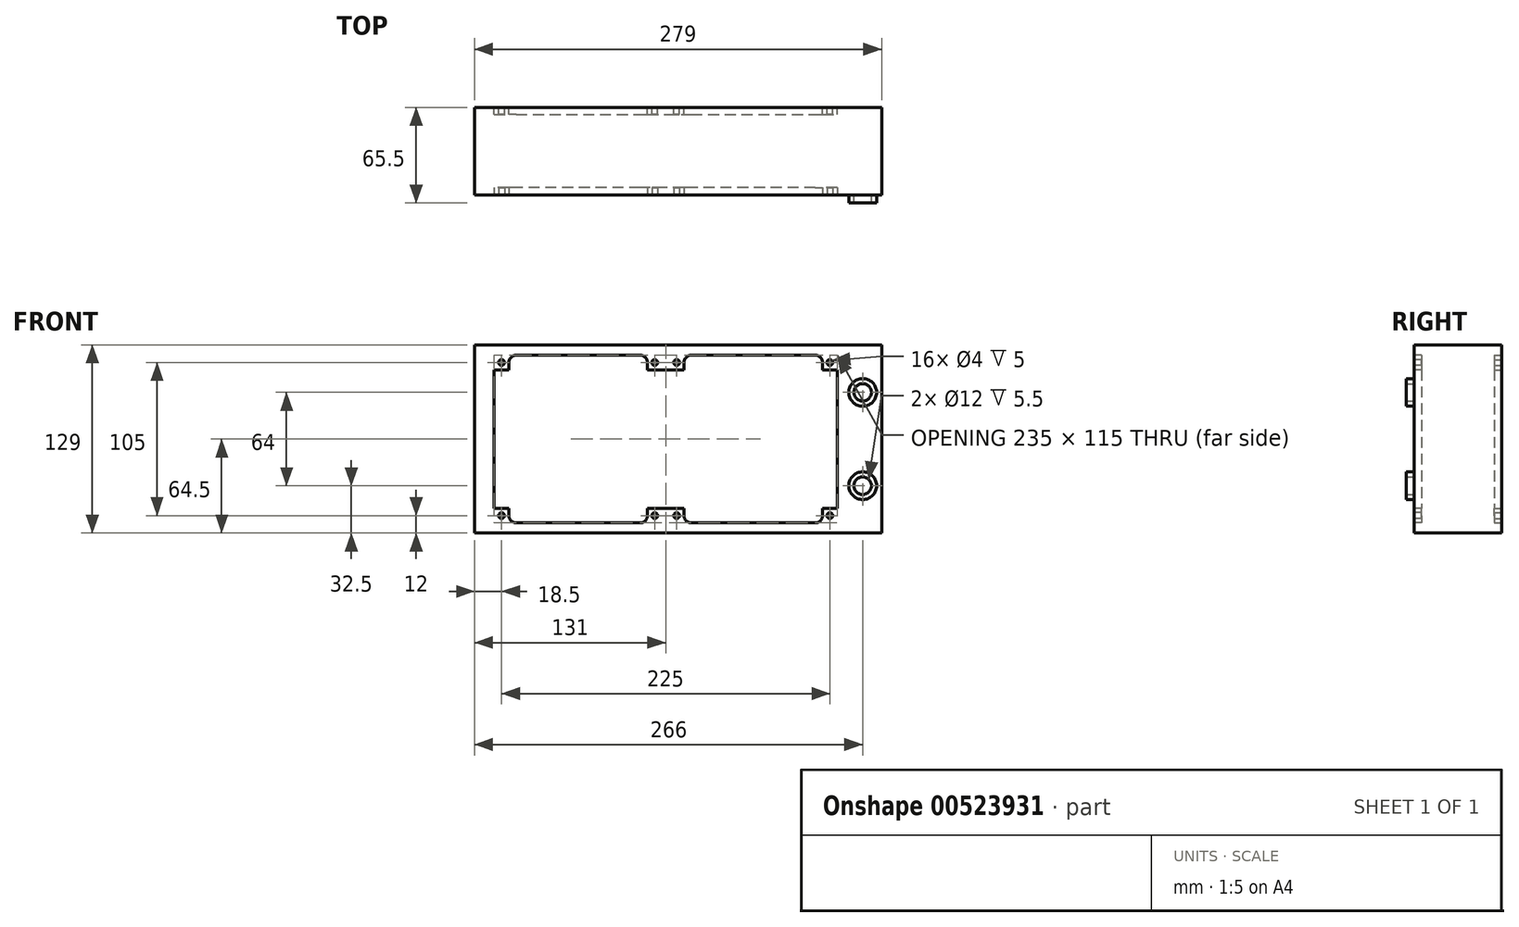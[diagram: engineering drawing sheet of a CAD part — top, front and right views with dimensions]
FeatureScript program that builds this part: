
annotation { "Feature Type Name" : "Feature", "Feature Type Description" : "" }
export const myFeature = defineFeature(function(context is Context, id is Id, definition is map)
    precondition{}
    {
        {
            var Q0;
            Q0=qCreatedBy(makeId("Front.planeOp"),FACE);
            var sketch = newSketch(context, id + "F0", { "sketchPlane" : qUnion([Q0])});
            skLineSegment(sketch, "E0.bottom", {"start": v(0, 64.5) * mm, "end": v(279, 64.5) * mm});
            skLineSegment(sketch, "E0.top", {"start": v(0, -64.5) * mm, "end": v(279, -64.5) * mm});
            skLineSegment(sketch, "E0.left", {"start": v(0, 64.5) * mm, "end": v(0, -64.5) * mm});
            skLineSegment(sketch, "E0.right", {"start": v(279, 64.5) * mm, "end": v(279, -64.5) * mm});
            skSolve(sketch);
        }
        {
            var Q0;
            Q0=qSketchRegion(id+"F0",true);
            extrude(context, id + "F1", {"entities" : qUnion([Q0]), "depth" : 60 * mm});
        }
        {
            var Q0;
            Q0=makeQuery(id+"F1.opExtrude","CAP_FACE",FACE,{"disambiguationData":[OSD([sQuery(id+"F0.wireOp",EDGE,"E0.bottom"),sQuery(id+"F0.wireOp",EDGE,"E0.top"),sQuery(id+"F0.wireOp",EDGE,"E0.left"),sQuery(id+"F0.wireOp",EDGE,"E0.right")])],"isStart":false});
            var sketch = newSketch(context, id + "F2", { "sketchPlane" : qUnion([Q0])});
            skCircle(sketch, "E1", {"center": v(266, -32) * mm, "radius": 9.5 * mm});
            skCircle(sketch, "E2", {"center": v(266, 32) * mm, "radius": 9.5 * mm});
            skLineSegment(sketch, "E3", {"start": v(0, 0) * mm, "end": v(279, 0) * mm, "construction": true});
            skCircle(sketch, "E4", {"center": v(266, 32) * mm, "radius": 6 * mm});
            skCircle(sketch, "E5", {"center": v(266, -32) * mm, "radius": 6 * mm});
            skSolve(sketch);
        }
        {
            var Q0;
            Q0=qSketchRegion(id+"F2",true);
            extrude(context, id + "F3", {"entities" : qUnion([Q0]), "operationType" : NewBodyOperationType.ADD, "depth" : 5.5 * mm});
        }
        {
            var Q0;
            {var subQ0=sQuery(id+"F0.wireOp",EDGE,"E0.right");var subQ1=sQuery(id+"F0.wireOp",EDGE,"E0.left");var subQ2=sQuery(id+"F0.wireOp",EDGE,"E0.top");var subQ3=sQuery(id+"F0.wireOp",EDGE,"E0.bottom");Q0=makeQuery(id+"F3.boolean.opBoolean","SPLIT",FACE,{"disambiguationData":[TD([makeQuery(id+"F1.opExtrude","SWEPT_FACE",FACE,{"disambiguationData":[OSD([subQ3])]})])],"derivedFrom":makeQuery(id+"F1.opExtrude","CAP_FACE",FACE,{"disambiguationData":[OSD([subQ3,subQ2,subQ1,subQ0])],"isStart":false})});}
            var sketch = newSketch(context, id + "F4", { "sketchPlane" : qUnion([Q0])});
            skCircle(sketch, "E6", {"center": v(18.5, 52.5) * mm, "radius": 2 * mm});
            skCircle(sketch, "E7", {"center": v(123.5, 52.5) * mm, "radius": 2 * mm});
            skCircle(sketch, "E8", {"center": v(138.5, 52.5) * mm, "radius": 2 * mm});
            skCircle(sketch, "E9", {"center": v(243.5, 52.5) * mm, "radius": 2 * mm});
            skLineSegment(sketch, "E10", {"start": v(13.5, 47.5) * mm, "end": v(13.5, 0) * mm});
            skLineSegment(sketch, "E11", {"start": v(248.5, 0) * mm, "end": v(248.5, 47.5) * mm});
            skLineSegment(sketch, "E12", {"start": v(248.5, 47.5) * mm, "end": v(238.5, 47.5) * mm});
            skLineSegment(sketch, "E13", {"start": v(238.5, 47.5) * mm, "end": v(238.5, 52.5) * mm});
            skLineSegment(sketch, "E14", {"start": v(233.5, 57.5) * mm, "end": v(148.5, 57.5) * mm});
            skLineSegment(sketch, "E15", {"start": v(143.5, 52.5) * mm, "end": v(143.5, 47.5) * mm});
            skLineSegment(sketch, "E16", {"start": v(143.5, 47.5) * mm, "end": v(118.5, 47.5) * mm});
            skLineSegment(sketch, "E17", {"start": v(118.5, 47.5) * mm, "end": v(118.5, 52.5) * mm});
            skLineSegment(sketch, "E18", {"start": v(113.5, 57.5) * mm, "end": v(28.5, 57.5) * mm});
            skLineSegment(sketch, "E19", {"start": v(23.5, 52.5) * mm, "end": v(23.5, 47.5) * mm});
            skLineSegment(sketch, "E20", {"start": v(23.5, 47.5) * mm, "end": v(13.5, 47.5) * mm});
            skLineSegment(sketch, "E21", {"start": v(0, 0) * mm, "end": v(279, 0) * mm, "construction": true});
            skPoint(sketch, "E22.visualSharp", {"position": v(143.5, 57.5) * mm});
            skArc(sketch, "E22.filletArc", {"start": v(148.5, 57.5) * mm, "mid": v(144.96, 56.04) * mm, "end": v(143.5, 52.5) * mm});
            skPoint(sketch, "E23.visualSharp", {"position": v(118.5, 57.5) * mm});
            skArc(sketch, "E23.filletArc", {"start": v(118.5, 52.5) * mm, "mid": v(117.04, 56.04) * mm, "end": v(113.5, 57.5) * mm});
            skPoint(sketch, "E24.visualSharp", {"position": v(238.5, 57.5) * mm});
            skArc(sketch, "E24.filletArc", {"start": v(238.5, 52.5) * mm, "mid": v(237.04, 56.04) * mm, "end": v(233.5, 57.5) * mm});
            skPoint(sketch, "E25.visualSharp", {"position": v(23.5, 57.5) * mm});
            skArc(sketch, "E25.filletArc", {"start": v(28.5, 57.5) * mm, "mid": v(24.96, 56.04) * mm, "end": v(23.5, 52.5) * mm});
            skCircle(sketch, "E26.MirrorC", {"center": v(243.5, -52.5) * mm, "radius": 2 * mm});
            skLineSegment(sketch, "E27.MirrorCS", {"start": v(248.5, 0) * mm, "end": v(248.5, -47.5) * mm});
            skLineSegment(sketch, "E28.MirrorCS", {"start": v(248.5, -47.5) * mm, "end": v(238.5, -47.5) * mm});
            skLineSegment(sketch, "E29.MirrorCS", {"start": v(238.5, -47.5) * mm, "end": v(238.5, -52.5) * mm});
            skArc(sketch, "E30.MirrorCS", {"start": v(238.5, -52.5) * mm, "mid": v(237.04, -56.04) * mm, "end": v(233.5, -57.5) * mm});
            skLineSegment(sketch, "E31.MirrorCS", {"start": v(233.5, -57.5) * mm, "end": v(148.5, -57.5) * mm});
            skArc(sketch, "E32.MirrorCS", {"start": v(148.5, -57.5) * mm, "mid": v(144.96, -56.04) * mm, "end": v(143.5, -52.5) * mm});
            skLineSegment(sketch, "E33.MirrorCS", {"start": v(143.5, -52.5) * mm, "end": v(143.5, -47.5) * mm});
            skCircle(sketch, "E34.MirrorC", {"center": v(138.5, -52.5) * mm, "radius": 2 * mm});
            skCircle(sketch, "E35.MirrorC", {"center": v(123.5, -52.5) * mm, "radius": 2 * mm});
            skLineSegment(sketch, "E36.MirrorCS", {"start": v(143.5, -47.5) * mm, "end": v(118.5, -47.5) * mm});
            skCircle(sketch, "E37.MirrorC", {"center": v(18.5, -52.5) * mm, "radius": 2 * mm});
            skLineSegment(sketch, "E38.MirrorCS", {"start": v(118.5, -47.5) * mm, "end": v(118.5, -52.5) * mm});
            skArc(sketch, "E39.MirrorCS", {"start": v(118.5, -52.5) * mm, "mid": v(117.04, -56.04) * mm, "end": v(113.5, -57.5) * mm});
            skLineSegment(sketch, "E40.MirrorCS", {"start": v(113.5, -57.5) * mm, "end": v(28.5, -57.5) * mm});
            skArc(sketch, "E41.MirrorCS", {"start": v(28.5, -57.5) * mm, "mid": v(24.96, -56.04) * mm, "end": v(23.5, -52.5) * mm});
            skLineSegment(sketch, "E42.MirrorCS", {"start": v(23.5, -52.5) * mm, "end": v(23.5, -47.5) * mm});
            skLineSegment(sketch, "E43.MirrorCS", {"start": v(13.5, -47.5) * mm, "end": v(13.5, 0) * mm});
            skLineSegment(sketch, "E44.MirrorCS", {"start": v(23.5, -47.5) * mm, "end": v(13.5, -47.5) * mm});
            skSolve(sketch);
        }
        {
            var Q0;
            Q0=qSketchRegion(id+"F4",true);
            extrude(context, id + "F5", {"entities" : qUnion([Q0]), "operationType" : NewBodyOperationType.REMOVE, "oppositeDirection" : true, "depth" : 5 * mm});
        }
        {
            var Q0;
            Q0=makeQuery(id+"F1.opExtrude","CAP_FACE",FACE,{"disambiguationData":[OSD([sQuery(id+"F0.wireOp",EDGE,"E0.bottom"),sQuery(id+"F0.wireOp",EDGE,"E0.top"),sQuery(id+"F0.wireOp",EDGE,"E0.left"),sQuery(id+"F0.wireOp",EDGE,"E0.right")])],"isStart":true});
            var sketch = newSketch(context, id + "F6", { "sketchPlane" : qUnion([Q0])});
            skCircle(sketch, "E45", {"center": v(-243.5, 52.5) * mm, "radius": 2 * mm});
            skCircle(sketch, "E46", {"center": v(-138.5, 52.5) * mm, "radius": 2 * mm});
            skCircle(sketch, "E47", {"center": v(-123.5, 52.5) * mm, "radius": 2 * mm});
            skCircle(sketch, "E48", {"center": v(-18.5, 52.5) * mm, "radius": 2 * mm});
            skLineSegment(sketch, "E49", {"start": v(-248.5, 47.5) * mm, "end": v(-248.5, 0) * mm});
            skLineSegment(sketch, "E50", {"start": v(-13.5, 0) * mm, "end": v(-13.5, 47.5) * mm});
            skLineSegment(sketch, "E51", {"start": v(-13.5, 47.5) * mm, "end": v(-23.5, 47.5) * mm});
            skLineSegment(sketch, "E52", {"start": v(-23.5, 47.5) * mm, "end": v(-23.5, 52.5) * mm});
            skLineSegment(sketch, "E53", {"start": v(-28.5, 57.5) * mm, "end": v(-113.5, 57.5) * mm});
            skLineSegment(sketch, "E54", {"start": v(-118.5, 52.5) * mm, "end": v(-118.5, 47.5) * mm});
            skLineSegment(sketch, "E55", {"start": v(-118.5, 47.5) * mm, "end": v(-143.5, 47.5) * mm});
            skLineSegment(sketch, "E56", {"start": v(-143.5, 47.5) * mm, "end": v(-143.5, 52.5) * mm});
            skLineSegment(sketch, "E57", {"start": v(-148.5, 57.5) * mm, "end": v(-233.5, 57.5) * mm});
            skLineSegment(sketch, "E58", {"start": v(-238.5, 52.5) * mm, "end": v(-238.5, 47.5) * mm});
            skLineSegment(sketch, "E59", {"start": v(-238.5, 47.5) * mm, "end": v(-248.5, 47.5) * mm});
            skLineSegment(sketch, "E60", {"start": v(-279, 0) * mm, "end": v(0, 0) * mm, "construction": true});
            skPoint(sketch, "E61.visualSharp", {"position": v(-118.5, 57.5) * mm});
            skArc(sketch, "E61.filletArc", {"start": v(-113.5, 57.5) * mm, "mid": v(-117.04, 56.04) * mm, "end": v(-118.5, 52.5) * mm});
            skPoint(sketch, "E62.visualSharp", {"position": v(-143.5, 57.5) * mm});
            skArc(sketch, "E62.filletArc", {"start": v(-143.5, 52.5) * mm, "mid": v(-144.96, 56.04) * mm, "end": v(-148.5, 57.5) * mm});
            skPoint(sketch, "E63.visualSharp", {"position": v(-23.5, 57.5) * mm});
            skArc(sketch, "E63.filletArc", {"start": v(-23.5, 52.5) * mm, "mid": v(-24.96, 56.04) * mm, "end": v(-28.5, 57.5) * mm});
            skPoint(sketch, "E64.visualSharp", {"position": v(-238.5, 57.5) * mm});
            skArc(sketch, "E64.filletArc", {"start": v(-233.5, 57.5) * mm, "mid": v(-237.04, 56.04) * mm, "end": v(-238.5, 52.5) * mm});
            skCircle(sketch, "E65.MirrorC", {"center": v(-18.5, -52.5) * mm, "radius": 2 * mm});
            skLineSegment(sketch, "E66.MirrorCS", {"start": v(-13.5, 0) * mm, "end": v(-13.5, -47.5) * mm});
            skLineSegment(sketch, "E67.MirrorCS", {"start": v(-13.5, -47.5) * mm, "end": v(-23.5, -47.5) * mm});
            skLineSegment(sketch, "E68.MirrorCS", {"start": v(-23.5, -47.5) * mm, "end": v(-23.5, -52.5) * mm});
            skArc(sketch, "E69.MirrorCS", {"start": v(-23.5, -52.5) * mm, "mid": v(-24.96, -56.04) * mm, "end": v(-28.5, -57.5) * mm});
            skLineSegment(sketch, "E70.MirrorCS", {"start": v(-28.5, -57.5) * mm, "end": v(-113.5, -57.5) * mm});
            skArc(sketch, "E71.MirrorCS", {"start": v(-113.5, -57.5) * mm, "mid": v(-117.04, -56.04) * mm, "end": v(-118.5, -52.5) * mm});
            skLineSegment(sketch, "E72.MirrorCS", {"start": v(-118.5, -52.5) * mm, "end": v(-118.5, -47.5) * mm});
            skCircle(sketch, "E73.MirrorC", {"center": v(-123.5, -52.5) * mm, "radius": 2 * mm});
            skCircle(sketch, "E74.MirrorC", {"center": v(-138.5, -52.5) * mm, "radius": 2 * mm});
            skLineSegment(sketch, "E75.MirrorCS", {"start": v(-118.5, -47.5) * mm, "end": v(-143.5, -47.5) * mm});
            skCircle(sketch, "E76.MirrorC", {"center": v(-243.5, -52.5) * mm, "radius": 2 * mm});
            skLineSegment(sketch, "E77.MirrorCS", {"start": v(-143.5, -47.5) * mm, "end": v(-143.5, -52.5) * mm});
            skArc(sketch, "E78.MirrorCS", {"start": v(-143.5, -52.5) * mm, "mid": v(-144.96, -56.04) * mm, "end": v(-148.5, -57.5) * mm});
            skLineSegment(sketch, "E79.MirrorCS", {"start": v(-148.5, -57.5) * mm, "end": v(-233.5, -57.5) * mm});
            skArc(sketch, "E80.MirrorCS", {"start": v(-233.5, -57.5) * mm, "mid": v(-237.04, -56.04) * mm, "end": v(-238.5, -52.5) * mm});
            skLineSegment(sketch, "E81.MirrorCS", {"start": v(-238.5, -52.5) * mm, "end": v(-238.5, -47.5) * mm});
            skLineSegment(sketch, "E82.MirrorCS", {"start": v(-248.5, -47.5) * mm, "end": v(-248.5, 0) * mm});
            skLineSegment(sketch, "E83.MirrorCS", {"start": v(-238.5, -47.5) * mm, "end": v(-248.5, -47.5) * mm});
            skSolve(sketch);
        }
        {
            var Q0;
            Q0=qSketchRegion(id+"F6",true);
            extrude(context, id + "F7", {"entities" : qUnion([Q0]), "operationType" : NewBodyOperationType.REMOVE, "oppositeDirection" : true, "depth" : 5 * mm});
        }
    });
